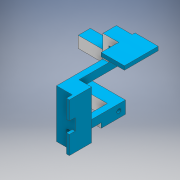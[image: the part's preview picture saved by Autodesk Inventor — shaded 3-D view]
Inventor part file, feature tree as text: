
AUTODESK INVENTOR PART (.ipt)
format: ipt  version: 2018.3 (Build 223284000, 284)  size: 412,160 bytes
history: native  units: mm
features: extrude x29, sketch x29, other x2
ambient origin geometry x8: Origin, YZ Plane, XZ Plane, XY Plane, X Axis, Y Axis, Z Axis, Center Point
bodies: Body1 (feature_tree)
feature tree (60):
  other  "Sólido1"
  extrude  "Extrusión1"  Depth=10.0mm TaperAngle=0.0deg
  extrude  "Extrusión2"  Depth=33.0mm TaperAngle=0.0deg
  extrude  "Extrusión3"  Depth=29.0mm TaperAngle=0.0deg
  extrude  "Extrusión4"  Depth=21.0mm
  extrude  "Extrusión5"  Depth=4.0mm TaperAngle=0.0deg
  extrude  "Extrusión6"  Depth=37.0mm TaperAngle=0.0deg
  extrude  "Extrusión7"  Depth=94.0mm TaperAngle=0.0deg
  extrude  "Extrusión8"  Depth=15.0mm
  extrude  "Extrusión9"  Depth=64.0mm TaperAngle=0.0deg
  extrude  "Extrusión10"  Depth=10.0mm
  extrude  "Extrusión11"  Depth=64.0mm TaperAngle=0.0deg
  extrude  "Extrusión13"  Depth=10.0mm
  extrude  "Extrusión14"  Depth=10.0mm
  extrude  "Extrusión15"  Depth=19.0mm TaperAngle=0.0deg
  extrude  "Extrusión17"  Depth=19.0mm TaperAngle=0.0deg
  extrude  "Extrusión18"  Depth=15.0mm TaperAngle=0.0deg
  extrude  "Extrusión19"  Depth=3.0mm
  extrude  "Extrusión20"  Depth=6.0mm TaperAngle=0.0deg
  extrude  "Extrusión21"  Depth=40.0mm TaperAngle=0.0deg
  extrude  "Extrusión22"  Depth=30.0mm TaperAngle=0.0deg
  extrude  "Extrusión23"  Depth=6.25mm TaperAngle=0.0deg
  extrude  "Extrusión24"  Depth=7.0mm TaperAngle=0.0deg
  extrude  "Extrusión25"  [1 undecoded]
  extrude  "Extrusión26"  [1 undecoded]
  extrude  "Extrusión27"  [1 undecoded]
  extrude  "Extrusión28"  [1 undecoded]
  extrude  "Extrusión29"  [1 undecoded]
  extrude  "Extrusión30"  [1 undecoded]
  extrude  "Extrusión31"  [1 undecoded]
  sketch  "Boceto1"  dims[d0=18.0mm d1=0.0mm d2=10.0mm d3=0.0mm]
  sketch  "Boceto2"  dims[d6=3.0mm d7=33.0mm d8=0.0mm]
  sketch  "Boceto4"  dims[d9=35.0mm d10=29.0mm d11=0.0mm]
  sketch  "Boceto5"  dims[d12=2.0mm d13=21.0mm]
  sketch  "Boceto6"  dims[d14=20.0mm d15=4.0mm d16=0.0mm]
  sketch  "Boceto7"  dims[d17=8.0mm d18=0.0mm d19=37.0mm d20=0.0mm]
  sketch  "Boceto8"  dims[d21=2.0mm d22=94.0mm d23=0.0mm]
  sketch  "Boceto9"  dims[d30=5.0mm d31=15.0mm]
  sketch  "Boceto12"  dims[d32=15.0mm d33=64.0mm d34=0.0mm]
  sketch  "Boceto13"  dims[d35=64.0mm d36=0.0mm d38=10.0mm]
  sketch  "Boceto15"  dims[d40=15.0mm d41=64.0mm d42=0.0mm]
  sketch  "Boceto17"  dims[d48=46.25mm d49=10.0mm]
  sketch  "Boceto18"  dims[d50=23.0mm d51=0.0mm d52=10.0mm]
  sketch  "Boceto19"  dims[d53=19.0mm d54=0.0mm d58=19.0mm d59=0.0mm]
  sketch  "Boceto20"  dims[d68=19.0mm d69=0.0mm d70=19.0mm d71=0.0mm]
  sketch  "Boceto21"  dims[d73=19.0mm d74=0.0mm d76=15.0mm d77=0.0mm]
  sketch  "Boceto22"  dims[d78=4.0mm d79=0.0mm d80=3.0mm]
  sketch  "Boceto23"  dims[d81=6.0mm d82=0.0mm d87=6.0mm d88=0.0mm]
  sketch  "Boceto24"  dims[d89=17.0mm d90=0.0mm d91=40.0mm d92=0.0mm]
  sketch  "Boceto25"  dims[d93=12.5mm d94=30.0mm d95=0.0mm]
  sketch  "Boceto26"  dims[d96=46.75mm d97=0.0mm d98=6.25mm d99=0.0mm]
  sketch  "Boceto27"  dims[d100=17.0mm d101=0.0mm d102=7.0mm d103=0.0mm]
  sketch  "Boceto28"  dims[d104=8.0mm d105=0.0mm]
  sketch  "Boceto29"
  sketch  "Boceto30"
  sketch  "Boceto31"
  sketch  "Boceto32"
  sketch  "Boceto33"
  sketch  "Boceto34"
  other  "Saliente-Extruir7"
note: 7 required parameter values undecoded (feature->parameter linkage not recoverable at this tier; creation-order binding heuristic only, values carry confidence <= 0.55)
